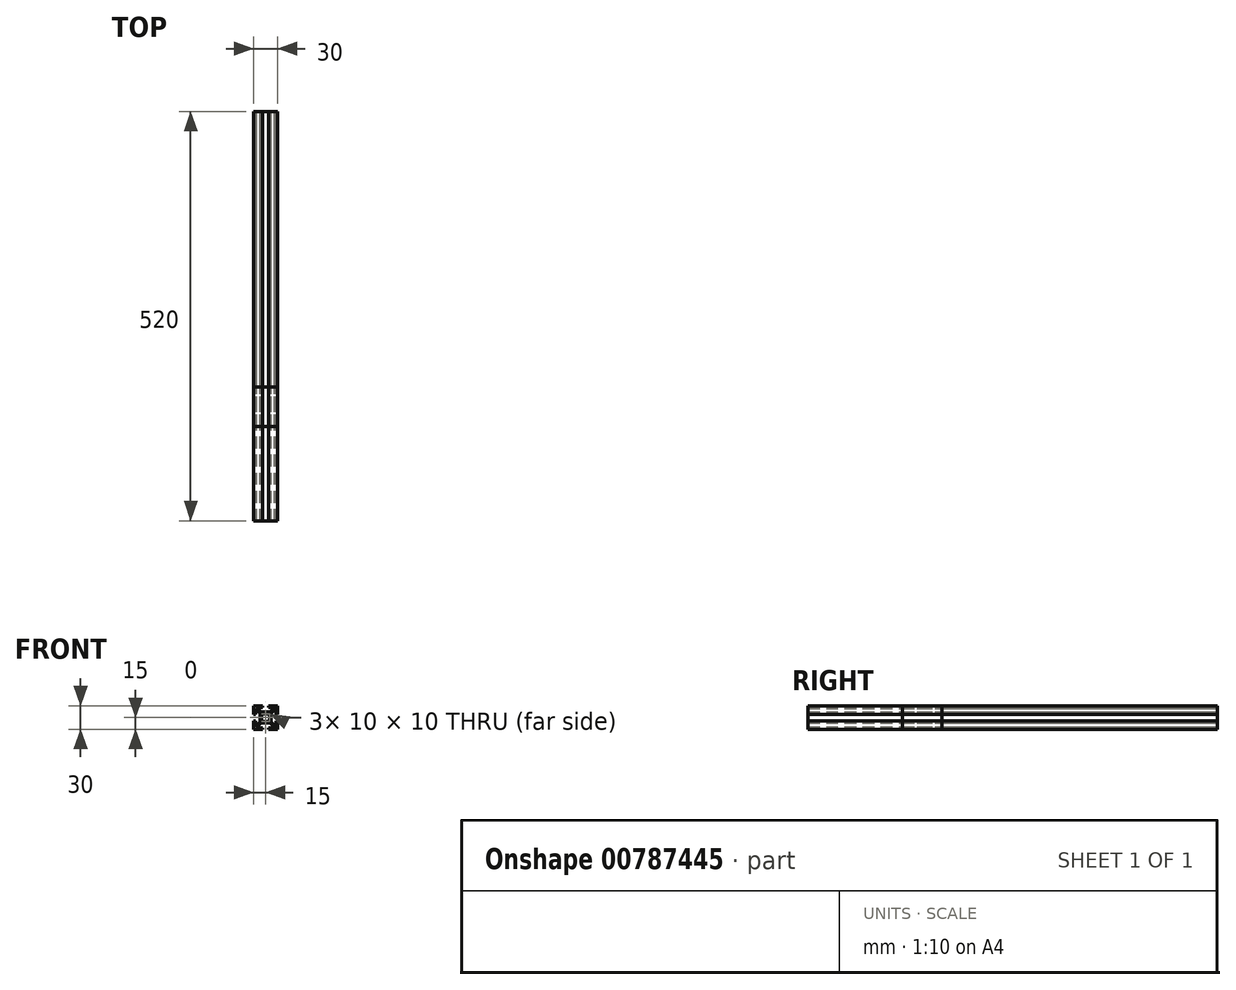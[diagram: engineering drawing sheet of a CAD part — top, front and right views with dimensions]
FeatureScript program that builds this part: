
annotation { "Feature Type Name" : "Feature", "Feature Type Description" : "" }
export const myFeature = defineFeature(function(context is Context, id is Id, definition is map)
    precondition{}
    {
        {
            var Q0;
            Q0=qCreatedBy(makeId("Front.planeOp"),FACE);
            var sketch = newSketch(context, id + "F0", { "sketchPlane" : qUnion([Q0])});
            skLineSegment(sketch, "E0.bottom", {"start": v(5, -5) * mm, "end": v(-5, -5) * mm});
            skLineSegment(sketch, "E0.top", {"start": v(5, 5) * mm, "end": v(-5, 5) * mm});
            skLineSegment(sketch, "E0.left", {"start": v(5, -5) * mm, "end": v(5, 5) * mm});
            skLineSegment(sketch, "E0.right", {"start": v(-5, -5) * mm, "end": v(-5, 5) * mm});
            skPoint(sketch, "E0.middle", {"position": v(0, 0) * mm});
            skLineSegment(sketch, "E1.bottom", {"start": v(-15, 15) * mm, "end": v(-4, 15) * mm});
            skLineSegment(sketch, "E1.top", {"start": v(-15, -15) * mm, "end": v(-4, -15) * mm});
            skLineSegment(sketch, "E1.left", {"start": v(-15, 15) * mm, "end": v(-15, 4) * mm});
            skLineSegment(sketch, "E1.right", {"start": v(15, 15) * mm, "end": v(15, 4) * mm});
            skLineSegment(sketch, "E2", {"start": v(-15, 4) * mm, "end": v(-13, 4) * mm});
            skLineSegment(sketch, "E3", {"start": v(-13, 4) * mm, "end": v(-13, 11.5) * mm});
            skLineSegment(sketch, "E4", {"start": v(-13, 11.5) * mm, "end": v(-7, 5.5) * mm});
            skLineSegment(sketch, "E5", {"start": v(-7, 5.5) * mm, "end": v(-7, -5.5) * mm});
            skLineSegment(sketch, "E6", {"start": v(-7, -5.5) * mm, "end": v(-13, -11.5) * mm});
            skLineSegment(sketch, "E7", {"start": v(-13, -11.5) * mm, "end": v(-13, -4) * mm});
            skLineSegment(sketch, "E8", {"start": v(-13, -4) * mm, "end": v(-15, -4) * mm});
            skLineSegment(sketch, "E9", {"start": v(-30.6, 0) * mm, "end": v(36.58, 0) * mm, "construction": true});
            skLineSegment(sketch, "E10", {"start": v(0, -25.45) * mm, "end": v(0, 23.58) * mm, "construction": true});
            skLineSegment(sketch, "E11.1.0", {"start": v(-4, -15) * mm, "end": v(-4, -13) * mm});
            skLineSegment(sketch, "E11.1.1", {"start": v(-4, -13) * mm, "end": v(-11.5, -13) * mm});
            skLineSegment(sketch, "E11.1.2", {"start": v(-11.5, -13) * mm, "end": v(-5.5, -7) * mm});
            skLineSegment(sketch, "E11.1.3", {"start": v(-5.5, -7) * mm, "end": v(5.5, -7) * mm});
            skLineSegment(sketch, "E11.1.4", {"start": v(5.5, -7) * mm, "end": v(11.5, -13) * mm});
            skLineSegment(sketch, "E11.1.5", {"start": v(11.5, -13) * mm, "end": v(4, -13) * mm});
            skLineSegment(sketch, "E11.1.6", {"start": v(4, -13) * mm, "end": v(4, -15) * mm});
            skLineSegment(sketch, "E11.2.0", {"start": v(15, -4) * mm, "end": v(13, -4) * mm});
            skLineSegment(sketch, "E11.2.1", {"start": v(13, -4) * mm, "end": v(13, -11.5) * mm});
            skLineSegment(sketch, "E11.2.2", {"start": v(13, -11.5) * mm, "end": v(7, -5.5) * mm});
            skLineSegment(sketch, "E11.2.3", {"start": v(7, -5.5) * mm, "end": v(7, 5.5) * mm});
            skLineSegment(sketch, "E11.2.4", {"start": v(7, 5.5) * mm, "end": v(13, 11.5) * mm});
            skLineSegment(sketch, "E11.2.5", {"start": v(13, 11.5) * mm, "end": v(13, 4) * mm});
            skLineSegment(sketch, "E11.2.6", {"start": v(13, 4) * mm, "end": v(15, 4) * mm});
            skLineSegment(sketch, "E11.3.0", {"start": v(4, 15) * mm, "end": v(4, 13) * mm});
            skLineSegment(sketch, "E11.3.1", {"start": v(4, 13) * mm, "end": v(11.5, 13) * mm});
            skLineSegment(sketch, "E11.3.2", {"start": v(11.5, 13) * mm, "end": v(5.5, 7) * mm});
            skLineSegment(sketch, "E11.3.3", {"start": v(5.5, 7) * mm, "end": v(-5.5, 7) * mm});
            skLineSegment(sketch, "E11.3.4", {"start": v(-5.5, 7) * mm, "end": v(-11.5, 13) * mm});
            skLineSegment(sketch, "E11.3.5", {"start": v(-11.5, 13) * mm, "end": v(-4, 13) * mm});
            skLineSegment(sketch, "E11.3.6", {"start": v(-4, 13) * mm, "end": v(-4, 15) * mm});
            skLineSegment(sketch, "E12.trimOffspring", {"start": v(4, -15) * mm, "end": v(15, -15) * mm});
            skLineSegment(sketch, "E13.trimOffspring", {"start": v(15, -4) * mm, "end": v(15, -15) * mm});
            skLineSegment(sketch, "E14.trimOffspring", {"start": v(4, 15) * mm, "end": v(15, 15) * mm});
            skLineSegment(sketch, "E15.trimOffspring", {"start": v(-15, -4) * mm, "end": v(-15, -15) * mm});
            skSolve(sketch);
        }
        {
            var Q0;
            Q0=makeQuery(id+"F0.imprint","IMPRINT",FACE,{"disambiguationData":[TD([[makeQuery(id+"F0.imprint","IMPRINT",EDGE,{"derivedFrom":sQuery(id+"F0.wireOp",EDGE,"E0.bottom")}),1.0]])]});
            extrude(context, id + "F1", {"entities" : qUnion([Q0]), "depth" : 520 * mm, "offsetDistance" : 25 * mm});
        }
        {
            var Q0;
            Q0 = qSketchRegion(id + "F0", true);
            extrude(context, id + "F2", {"entities" : qUnion([Q0]), "depth" : 400 * mm, "offsetDistance" : 25 * mm});
        }
        {
            var Q0;
            Q0 = qSketchRegion(id + "F0", true);
            extrude(context, id + "F3", {"entities" : qUnion([Q0]), "depth" : 350 * mm, "offsetDistance" : 25 * mm});
        }
    });
